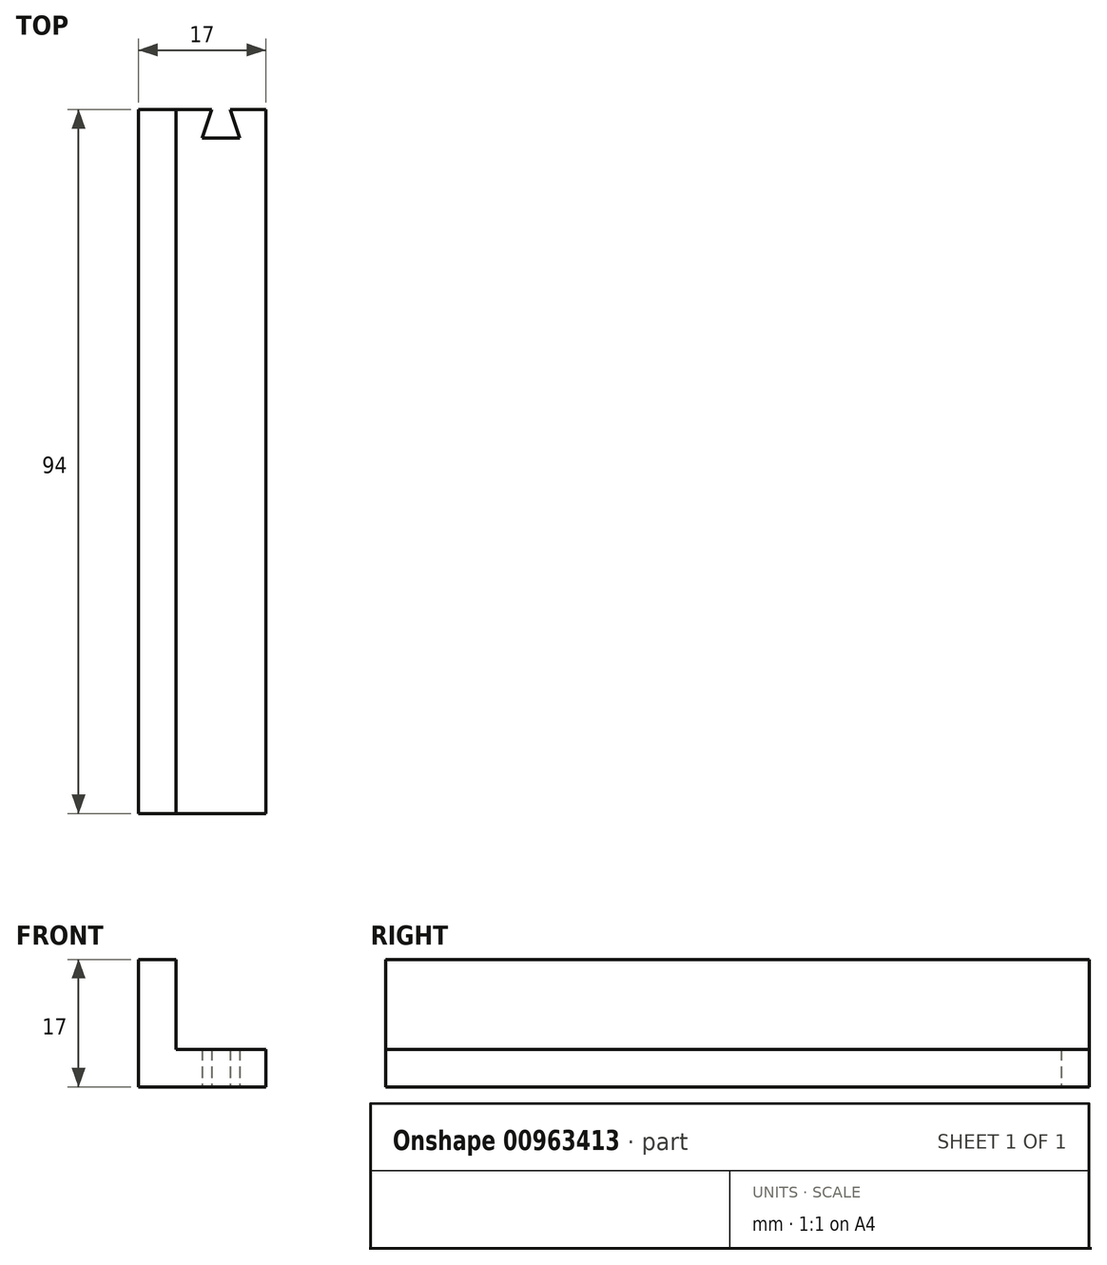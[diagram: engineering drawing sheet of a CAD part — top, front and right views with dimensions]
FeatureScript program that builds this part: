
annotation { "Feature Type Name" : "Feature", "Feature Type Description" : "" }
export const myFeature = defineFeature(function(context is Context, id is Id, definition is map)
    precondition{}
    {
        {
            var Q0;
            Q0=qCreatedBy(makeId("Top.planeOp"),FACE);
            var sketch = newSketch(context, id + "F0", { "sketchPlane" : qUnion([Q0])});
            skLineSegment(sketch, "E0.bottom", {"start": v(8.5, -47) * mm, "end": v(-8.5, -47) * mm});
            skLineSegment(sketch, "E0.top", {"start": v(8.5, 47) * mm, "end": v(-8.5, 47) * mm});
            skLineSegment(sketch, "E0.left", {"start": v(8.5, -47) * mm, "end": v(8.5, 47) * mm});
            skLineSegment(sketch, "E0.right", {"start": v(-8.5, -47) * mm, "end": v(-8.5, 47) * mm});
            skPoint(sketch, "E0.middle", {"position": v(0, 0) * mm});
            skPoint(sketch, "E1", {"position": v(-3.5, 47) * mm});
            skPoint(sketch, "E2", {"position": v(1.25, 47) * mm});
            skPoint(sketch, "E3", {"position": v(3.75, 47) * mm});
            skPoint(sketch, "E4", {"position": v(0, 47) * mm});
            skPoint(sketch, "E5", {"position": v(5, 47) * mm});
            skLineSegment(sketch, "E6", {"start": v(1.25, 47) * mm, "end": v(0, 43.25) * mm});
            skLineSegment(sketch, "E7", {"start": v(0, 43.25) * mm, "end": v(5, 43.25) * mm});
            skLineSegment(sketch, "E8", {"start": v(5, 43.25) * mm, "end": v(3.75, 47) * mm});
            skSolve(sketch);
        }
        {
            var Q0;
            Q0=makeQuery(id+"F0.imprint","IMPRINT",FACE,{"disambiguationData":[TD([[makeQuery(id+"F0.imprint","IMPRINT",EDGE,{"derivedFrom":sQuery(id+"F0.wireOp",EDGE,"E0.bottom")}),-1.0]])]});
            extrude(context, id + "F1", {"entities" : qUnion([Q0]), "depth" : 5 * mm, "offsetDistance" : 25 * mm});
        }
        {
            var Q0;
            Q0=makeQuery(id+"F1.opExtrude","CAP_FACE",FACE,{"disambiguationData":[OSD([sQuery(id+"F0.wireOp",EDGE,"E0.bottom"),sQuery(id+"F0.wireOp",EDGE,"E0.top"),sQuery(id+"F0.wireOp",EDGE,"E0.left"),sQuery(id+"F0.wireOp",EDGE,"E0.right"),sQuery(id+"F0.wireOp",EDGE,"rw5FdkIU-7Pyv-DcX8-fDZG-QsmjpqUQaUpg"),sQuery(id+"F0.wireOp",EDGE,"jVwzFZEz-LamF-PFxA-NCYc-S7eYUaHMYtTf"),sQuery(id+"F0.wireOp",EDGE,"HgkX7Yv0-hTDJ-ucJP-wwuC-oNEPRnFH2NnW"),sQuery(id+"F0.wireOp",EDGE,"0Pd2xpSO-AvzK-sIeG-jRaa-LW2rH33TRvBc")])],"isStart":false});
            var sketch = newSketch(context, id + "F2", { "sketchPlane" : qUnion([Q0])});
            skLineSegment(sketch, "E9.bottom", {"start": v(-8.5, 47) * mm, "end": v(-3.5, 47) * mm});
            skLineSegment(sketch, "E9.top", {"start": v(-8.5, -47) * mm, "end": v(-3.5, -47) * mm});
            skLineSegment(sketch, "E9.left", {"start": v(-8.5, 47) * mm, "end": v(-8.5, -47) * mm});
            skLineSegment(sketch, "E9.right", {"start": v(-3.5, 47) * mm, "end": v(-3.5, -47) * mm});
            skSolve(sketch);
        }
        {
            var Q0;
            Q0=makeQuery(id+"F2.imprint","IMPRINT",FACE,{"disambiguationData":[TD([[makeQuery(id+"F2.imprint","IMPRINT",EDGE,{"derivedFrom":sQuery(id+"F2.wireOp",EDGE,"E9.bottom")}),1.0]])]});
            extrude(context, id + "F3", {"entities" : qUnion([Q0]), "operationType" : NewBodyOperationType.ADD, "depth" : 12 * mm, "offsetDistance" : 25 * mm});
        }
    });
